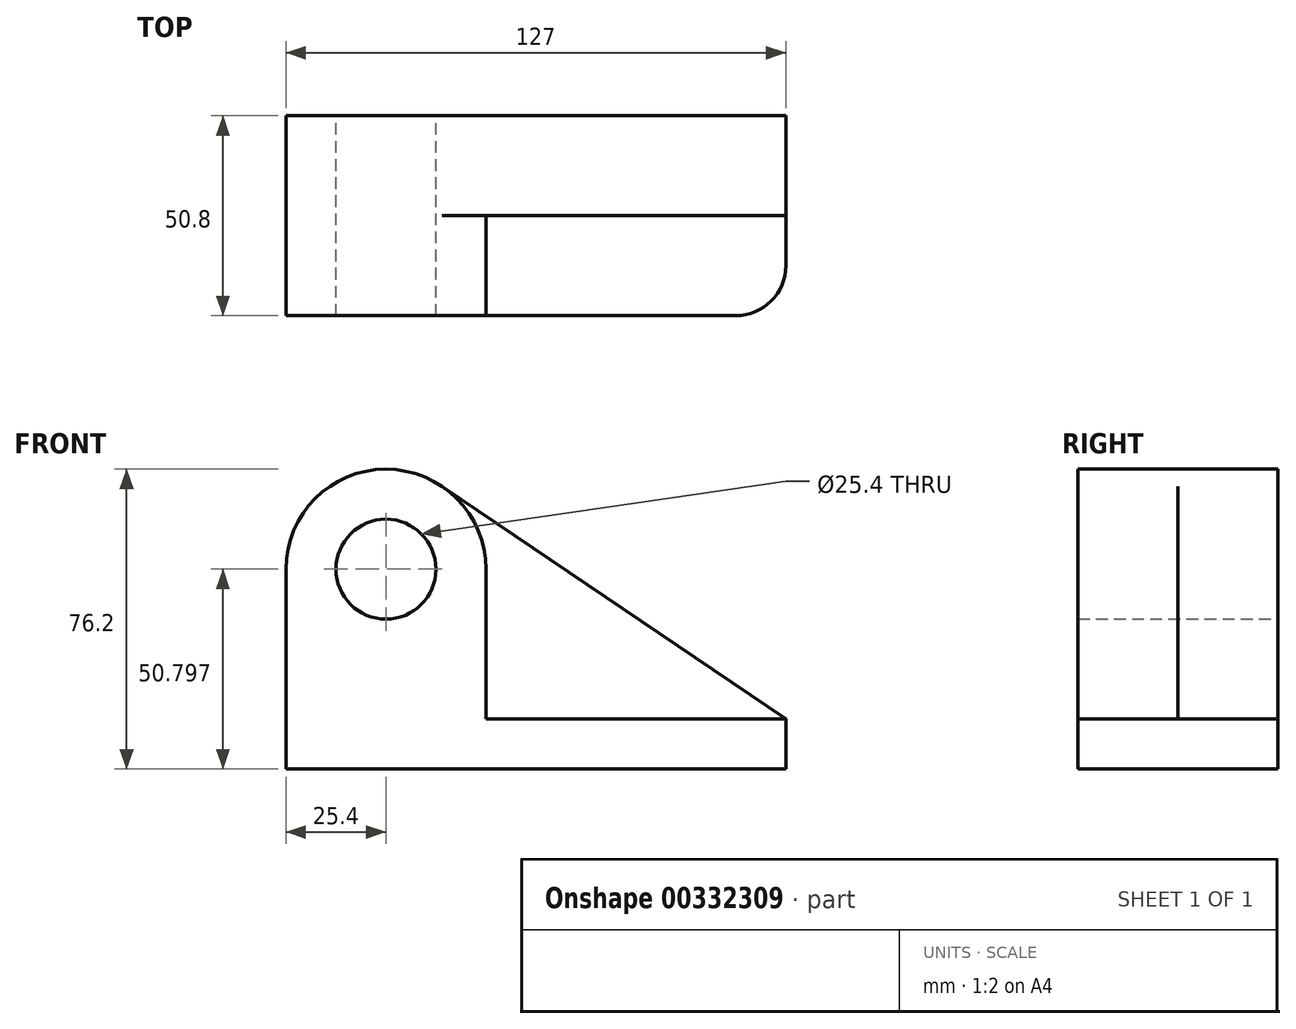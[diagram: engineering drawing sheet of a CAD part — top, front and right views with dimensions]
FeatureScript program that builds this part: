
annotation { "Feature Type Name" : "Feature", "Feature Type Description" : "" }
export const myFeature = defineFeature(function(context is Context, id is Id, definition is map)
    precondition{}
    {
        {
            var Q0;
            Q0=qCreatedBy(makeId("Front.planeOp"),FACE);
            var sketch = newSketch(context, id + "F0", { "sketchPlane" : qUnion([Q0])});
            skCircle(sketch, "E0", {"center": v(-38.39, 62.9) * mm, "radius": 12.7 * mm});
            skArc(sketch, "E1", {"start": v(-24.15, 83.94) * mm, "mid": v(-50.3, 85.35) * mm, "end": v(-63.79, 62.9) * mm});
            skLineSegment(sketch, "E2", {"start": v(-63.79, 62.9) * mm, "end": v(-63.79, 12.1) * mm});
            skLineSegment(sketch, "E3", {"start": v(-63.79, 12.1) * mm, "end": v(63.21, 12.1) * mm});
            skLineSegment(sketch, "E4", {"start": v(63.21, 12.1) * mm, "end": v(63.21, 24.8) * mm});
            skLineSegment(sketch, "E5", {"start": v(-24.15, 83.94) * mm, "end": v(63.21, 24.8) * mm});
            skSolve(sketch);
        }
        {
            var Q0;
            Q0=makeQuery(id+"F0.imprint","IMPRINT",FACE,{"disambiguationData":[TD([[makeQuery(id+"F0.imprint","IMPRINT",EDGE,{"derivedFrom":sQuery(id+"F0.wireOp",EDGE,"E0")}),-1.0]])]});
            extrude(context, id + "F1", {"entities" : qUnion([Q0]), "depth" : 25.4 * mm});
        }
        {
            var Q0;
            Q0=makeQuery(id+"F1.opExtrude","CAP_FACE",FACE,{"disambiguationData":[OSD([sQuery(id+"F0.wireOp",EDGE,"E0"),sQuery(id+"F0.wireOp",EDGE,"E1"),sQuery(id+"F0.wireOp",EDGE,"E2"),sQuery(id+"F0.wireOp",EDGE,"E3"),sQuery(id+"F0.wireOp",EDGE,"E4"),sQuery(id+"F0.wireOp",EDGE,"E5")])],"isStart":false});
            var sketch = newSketch(context, id + "F2", { "sketchPlane" : qUnion([Q0])});
            skCircle(sketch, "E6", {"center": v(-38.39, 62.9) * mm, "radius": 12.7 * mm});
            skArc(sketch, "E7", {"start": v(-12.99, 62.9) * mm, "mid": v(-38.39, 88.3) * mm, "end": v(-63.79, 62.9) * mm});
            skLineSegment(sketch, "E8", {"start": v(63.21, 24.8) * mm, "end": v(-12.99, 24.8) * mm});
            skLineSegment(sketch, "E9", {"start": v(-63.79, 62.9) * mm, "end": v(-63.79, 24.8) * mm});
            skLineSegment(sketch, "E10", {"start": v(-12.99, 62.9) * mm, "end": v(-12.99, 24.8) * mm});
            skSolve(sketch);
        }
        {
            var Q0;
            Q0=makeQuery(id+"F2.imprint","IMPRINT",FACE,{"disambiguationData":[TD([[makeQuery(id+"F2.imprint","IMPRINT",EDGE,{"derivedFrom":sQuery(id+"F2.wireOp",EDGE,"E6")}),-1.0]])]});
            extrude(context, id + "F3", {"entities" : qUnion([Q0]), "operationType" : NewBodyOperationType.ADD, "depth" : 25.4 * mm});
        }
        {
            var Q0;
            Q0=makeQuery(id+"F3.opExtrude","CAP_EDGE",EDGE,{"disambiguationData":[OSD([sQuery(id+"F0.wireOp",EDGE,"E4")])],"isStart":false});
            fillet(context, id + "F4", {"entities" : qUnion([Q0]), "radius" : 12.7 * mm, "tangentPropagation" : true, "allowEdgeOverflow" : false});
        }
    });
